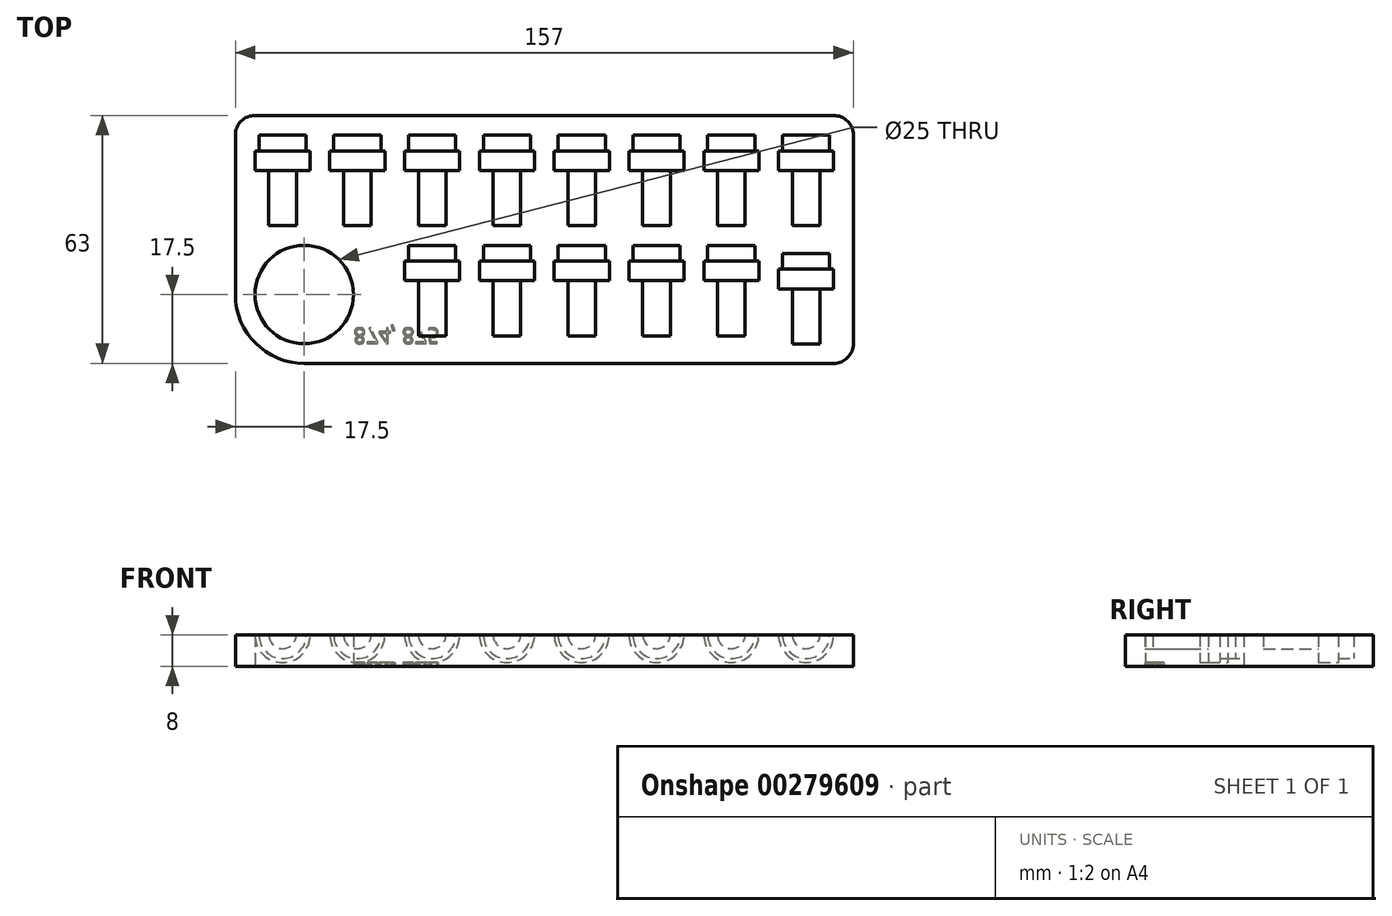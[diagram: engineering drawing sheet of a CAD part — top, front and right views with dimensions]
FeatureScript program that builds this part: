
annotation { "Feature Type Name" : "Feature", "Feature Type Description" : "" }
export const myFeature = defineFeature(function(context is Context, id is Id, definition is map)
    precondition{}
    {
        {
            var Q0;
            Q0=qCreatedBy(makeId("Top.planeOp"),FACE);
            var sketch = newSketch(context, id + "F0", { "sketchPlane" : qUnion([Q0])});
            skLineSegment(sketch, "E0.bottom", {"start": v(17.5, 0) * mm, "end": v(152, 0) * mm});
            skLineSegment(sketch, "E0.top", {"start": v(5, 63) * mm, "end": v(152, 63) * mm});
            skLineSegment(sketch, "E0.left", {"start": v(0, 17.5) * mm, "end": v(0, 58) * mm});
            skLineSegment(sketch, "E0.right", {"start": v(157, 5) * mm, "end": v(157, 58) * mm});
            skLineSegment(sketch, "E1.bottom", {"start": v(0, 0) * mm, "end": v(17.5, 0) * mm, "construction": true});
            skLineSegment(sketch, "E1.top", {"start": v(0, 17.5) * mm, "end": v(17.5, 17.5) * mm, "construction": true});
            skLineSegment(sketch, "E1.left", {"start": v(0, 0) * mm, "end": v(0, 17.5) * mm, "construction": true});
            skLineSegment(sketch, "E1.right", {"start": v(17.5, 0) * mm, "end": v(17.5, 17.5) * mm, "construction": true});
            skCircle(sketch, "E2", {"center": v(17.5, 17.5) * mm, "radius": 12.5 * mm});
            skPoint(sketch, "E3.visualSharp", {"position": v(0, 0) * mm});
            skArc(sketch, "E3.filletArc", {"start": v(0, 17.5) * mm, "mid": v(5.13, 5.13) * mm, "end": v(17.5, 0) * mm});
            skPoint(sketch, "E4.visualSharp", {"position": v(0, 63) * mm});
            skArc(sketch, "E4.filletArc", {"start": v(5, 63) * mm, "mid": v(1.46, 61.54) * mm, "end": v(0, 58) * mm});
            skPoint(sketch, "E5.visualSharp", {"position": v(157, 63) * mm});
            skArc(sketch, "E5.filletArc", {"start": v(157, 58) * mm, "mid": v(155.54, 61.54) * mm, "end": v(152, 63) * mm});
            skPoint(sketch, "E6.visualSharp", {"position": v(157, 0) * mm});
            skArc(sketch, "E6.filletArc", {"start": v(152, 0) * mm, "mid": v(155.54, 1.46) * mm, "end": v(157, 5) * mm});
            skSolve(sketch);
        }
        {
            var Q0;
            Q0=makeQuery(id+"F0.imprint","IMPRINT",FACE,{"disambiguationData":[TD([[makeQuery(id+"F0.imprint","IMPRINT",EDGE,{"derivedFrom":sQuery(id+"F0.wireOp",EDGE,"E0.bottom")}),1.0]])]});
            extrude(context, id + "F1", {"entities" : qUnion([Q0]), "depth" : 8 * mm});
        }
        {
            var Q0;
            Q0=makeQuery(id+"F1.opExtrude","CAP_FACE",FACE,{"disambiguationData":[OSD([sQuery(id+"F0.wireOp",EDGE,"E0.bottom"),sQuery(id+"F0.wireOp",EDGE,"E0.top"),sQuery(id+"F0.wireOp",EDGE,"E0.left"),sQuery(id+"F0.wireOp",EDGE,"E0.right"),sQuery(id+"F0.wireOp",EDGE,"E2"),sQuery(id+"F0.wireOp",EDGE,"E3.filletArc"),sQuery(id+"F0.wireOp",EDGE,"E4.filletArc"),sQuery(id+"F0.wireOp",EDGE,"E5.filletArc"),sQuery(id+"F0.wireOp",EDGE,"E6.filletArc")])],"isStart":false});
            var sketch = newSketch(context, id + "F2", { "sketchPlane" : qUnion([Q0])});
            skLineSegment(sketch, "E7.bottom", {"start": v(0, 0) * mm, "end": v(12, 0) * mm, "construction": true});
            skLineSegment(sketch, "E7.top", {"start": v(0, 35) * mm, "end": v(12, 35) * mm, "construction": true});
            skLineSegment(sketch, "E7.left", {"start": v(0, 0) * mm, "end": v(0, 35) * mm, "construction": true});
            skLineSegment(sketch, "E7.right", {"start": v(12, 0) * mm, "end": v(12, 35) * mm, "construction": true});
            skLineSegment(sketch, "E8.bottom", {"start": v(12, 35) * mm, "end": v(15.5, 35) * mm});
            skLineSegment(sketch, "E8.left", {"start": v(12, 35) * mm, "end": v(12, 49) * mm});
            skLineSegment(sketch, "E8.right", {"start": v(15.5, 35) * mm, "end": v(15.5, 49) * mm});
            skLineSegment(sketch, "E9.bottom", {"start": v(15.5, 49) * mm, "end": v(19, 49) * mm});
            skLineSegment(sketch, "E9.top", {"start": v(18, 54) * mm, "end": v(19, 54) * mm});
            skLineSegment(sketch, "E9.left", {"start": v(12, 49) * mm, "end": v(12, 54) * mm});
            skLineSegment(sketch, "E9.right", {"start": v(19, 49) * mm, "end": v(19, 54) * mm});
            skLineSegment(sketch, "E10.top", {"start": v(12, 58) * mm, "end": v(18, 58) * mm});
            skLineSegment(sketch, "E10.left", {"start": v(12, 54) * mm, "end": v(12, 58) * mm});
            skLineSegment(sketch, "E10.right", {"start": v(18, 54) * mm, "end": v(18, 58) * mm});
            skLineSegment(sketch, "E11", {"start": v(12, 35) * mm, "end": v(31, 35) * mm, "construction": true});
            skLineSegment(sketch, "E12.bottom", {"start": v(31, 35) * mm, "end": v(50, 35) * mm, "construction": true});
            skLineSegment(sketch, "E12.right", {"start": v(50, 35) * mm, "end": v(50, 30) * mm, "construction": true});
            skLineSegment(sketch, "E13.bottom", {"start": v(50, 35) * mm, "end": v(69, 35) * mm, "construction": true});
            skLineSegment(sketch, "E13.top", {"start": v(50, 30) * mm, "end": v(69, 30) * mm, "construction": true});
            skLineSegment(sketch, "E13.right", {"start": v(69, 35) * mm, "end": v(69, 30) * mm, "construction": true});
            skLineSegment(sketch, "E14.bottom", {"start": v(69, 35) * mm, "end": v(88, 35) * mm, "construction": true});
            skLineSegment(sketch, "E14.top", {"start": v(69, 30) * mm, "end": v(88, 30) * mm, "construction": true});
            skLineSegment(sketch, "E14.right", {"start": v(88, 35) * mm, "end": v(88, 30) * mm, "construction": true});
            skLineSegment(sketch, "E15.bottom", {"start": v(88, 35) * mm, "end": v(107, 35) * mm, "construction": true});
            skLineSegment(sketch, "E15.top", {"start": v(88, 30) * mm, "end": v(107, 30) * mm, "construction": true});
            skLineSegment(sketch, "E15.right", {"start": v(107, 35) * mm, "end": v(107, 30) * mm, "construction": true});
            skLineSegment(sketch, "E16.bottom", {"start": v(107, 35) * mm, "end": v(126, 35) * mm, "construction": true});
            skLineSegment(sketch, "E16.top", {"start": v(107, 30) * mm, "end": v(126, 30) * mm, "construction": true});
            skLineSegment(sketch, "E16.right", {"start": v(126, 35) * mm, "end": v(126, 30) * mm, "construction": true});
            skLineSegment(sketch, "E17.bottom", {"start": v(107, 35) * mm, "end": v(110.5, 35) * mm});
            skLineSegment(sketch, "E17.left", {"start": v(107, 35) * mm, "end": v(107, 49) * mm});
            skLineSegment(sketch, "E17.right", {"start": v(110.5, 35) * mm, "end": v(110.5, 49) * mm});
            skLineSegment(sketch, "E18.bottom", {"start": v(110.5, 49) * mm, "end": v(114, 49) * mm});
            skLineSegment(sketch, "E18.top", {"start": v(113, 54) * mm, "end": v(114, 54) * mm});
            skLineSegment(sketch, "E18.left", {"start": v(107, 49) * mm, "end": v(107, 54) * mm});
            skLineSegment(sketch, "E18.right", {"start": v(114, 49) * mm, "end": v(114, 54) * mm});
            skLineSegment(sketch, "E19.top", {"start": v(107, 58) * mm, "end": v(113, 58) * mm});
            skLineSegment(sketch, "E19.left", {"start": v(107, 54) * mm, "end": v(107, 58) * mm});
            skLineSegment(sketch, "E19.right", {"start": v(113, 54) * mm, "end": v(113, 58) * mm});
            skLineSegment(sketch, "E20.bottom", {"start": v(50, 35) * mm, "end": v(53.5, 35) * mm});
            skLineSegment(sketch, "E20.left", {"start": v(50, 35) * mm, "end": v(50, 49) * mm});
            skLineSegment(sketch, "E20.right", {"start": v(53.5, 35) * mm, "end": v(53.5, 49) * mm});
            skLineSegment(sketch, "E21.bottom", {"start": v(53.5, 49) * mm, "end": v(57, 49) * mm});
            skLineSegment(sketch, "E21.top", {"start": v(56, 54) * mm, "end": v(57, 54) * mm});
            skLineSegment(sketch, "E21.left", {"start": v(50, 49) * mm, "end": v(50, 54) * mm});
            skLineSegment(sketch, "E21.right", {"start": v(57, 49) * mm, "end": v(57, 54) * mm});
            skLineSegment(sketch, "E22.top", {"start": v(50, 58) * mm, "end": v(56, 58) * mm});
            skLineSegment(sketch, "E22.left", {"start": v(50, 54) * mm, "end": v(50, 58) * mm});
            skLineSegment(sketch, "E22.right", {"start": v(56, 54) * mm, "end": v(56, 58) * mm});
            skLineSegment(sketch, "E23.bottom", {"start": v(88, 35) * mm, "end": v(91.5, 35) * mm});
            skLineSegment(sketch, "E23.left", {"start": v(88, 35) * mm, "end": v(88, 49) * mm});
            skLineSegment(sketch, "E23.right", {"start": v(91.5, 35) * mm, "end": v(91.5, 49) * mm});
            skLineSegment(sketch, "E24.bottom", {"start": v(91.5, 49) * mm, "end": v(95, 49) * mm});
            skLineSegment(sketch, "E24.top", {"start": v(94, 54) * mm, "end": v(95, 54) * mm});
            skLineSegment(sketch, "E24.left", {"start": v(88, 49) * mm, "end": v(88, 54) * mm});
            skLineSegment(sketch, "E24.right", {"start": v(95, 49) * mm, "end": v(95, 54) * mm});
            skLineSegment(sketch, "E25.top", {"start": v(88, 58) * mm, "end": v(94, 58) * mm});
            skLineSegment(sketch, "E25.left", {"start": v(88, 54) * mm, "end": v(88, 58) * mm});
            skLineSegment(sketch, "E25.right", {"start": v(94, 54) * mm, "end": v(94, 58) * mm});
            skLineSegment(sketch, "E26.bottom", {"start": v(69, 35) * mm, "end": v(72.5, 35) * mm});
            skLineSegment(sketch, "E26.left", {"start": v(69, 35) * mm, "end": v(69, 49) * mm});
            skLineSegment(sketch, "E26.right", {"start": v(72.5, 35) * mm, "end": v(72.5, 49) * mm});
            skLineSegment(sketch, "E27.bottom", {"start": v(72.5, 49) * mm, "end": v(76, 49) * mm});
            skLineSegment(sketch, "E27.top", {"start": v(75, 54) * mm, "end": v(76, 54) * mm});
            skLineSegment(sketch, "E27.left", {"start": v(69, 49) * mm, "end": v(69, 54) * mm});
            skLineSegment(sketch, "E27.right", {"start": v(76, 49) * mm, "end": v(76, 54) * mm});
            skLineSegment(sketch, "E28.top", {"start": v(69, 58) * mm, "end": v(75, 58) * mm});
            skLineSegment(sketch, "E28.left", {"start": v(69, 54) * mm, "end": v(69, 58) * mm});
            skLineSegment(sketch, "E28.right", {"start": v(75, 54) * mm, "end": v(75, 58) * mm});
            skLineSegment(sketch, "E29.bottom", {"start": v(31, 35) * mm, "end": v(34.5, 35) * mm});
            skLineSegment(sketch, "E29.left", {"start": v(31, 35) * mm, "end": v(31, 49) * mm});
            skLineSegment(sketch, "E29.right", {"start": v(34.5, 35) * mm, "end": v(34.5, 49) * mm});
            skLineSegment(sketch, "E30.bottom", {"start": v(34.5, 49) * mm, "end": v(38, 49) * mm});
            skLineSegment(sketch, "E30.top", {"start": v(37, 54) * mm, "end": v(38, 54) * mm});
            skLineSegment(sketch, "E30.left", {"start": v(31, 49) * mm, "end": v(31, 54) * mm});
            skLineSegment(sketch, "E30.right", {"start": v(38, 49) * mm, "end": v(38, 54) * mm});
            skLineSegment(sketch, "E31.top", {"start": v(31, 58) * mm, "end": v(37, 58) * mm});
            skLineSegment(sketch, "E31.left", {"start": v(31, 54) * mm, "end": v(31, 58) * mm});
            skLineSegment(sketch, "E31.right", {"start": v(37, 54) * mm, "end": v(37, 58) * mm});
            skLineSegment(sketch, "E32.bottom", {"start": v(50, 7) * mm, "end": v(53.5, 7) * mm});
            skLineSegment(sketch, "E32.left", {"start": v(50, 7) * mm, "end": v(50, 21) * mm});
            skLineSegment(sketch, "E32.right", {"start": v(53.5, 7) * mm, "end": v(53.5, 21) * mm});
            skLineSegment(sketch, "E33.bottom", {"start": v(53.5, 21) * mm, "end": v(57, 21) * mm});
            skLineSegment(sketch, "E33.top", {"start": v(56, 26) * mm, "end": v(57, 26) * mm});
            skLineSegment(sketch, "E33.left", {"start": v(50, 21) * mm, "end": v(50, 26) * mm});
            skLineSegment(sketch, "E33.right", {"start": v(57, 21) * mm, "end": v(57, 26) * mm});
            skLineSegment(sketch, "E34.top", {"start": v(50, 30) * mm, "end": v(56, 30) * mm});
            skLineSegment(sketch, "E34.left", {"start": v(50, 26) * mm, "end": v(50, 30) * mm});
            skLineSegment(sketch, "E34.right", {"start": v(56, 26) * mm, "end": v(56, 30) * mm});
            skLineSegment(sketch, "E35.bottom", {"start": v(88, 7) * mm, "end": v(91.5, 7) * mm});
            skLineSegment(sketch, "E35.left", {"start": v(88, 7) * mm, "end": v(88, 21) * mm});
            skLineSegment(sketch, "E35.right", {"start": v(91.5, 7) * mm, "end": v(91.5, 21) * mm});
            skLineSegment(sketch, "E36.bottom", {"start": v(91.5, 21) * mm, "end": v(95, 21) * mm});
            skLineSegment(sketch, "E36.top", {"start": v(94, 26) * mm, "end": v(95, 26) * mm});
            skLineSegment(sketch, "E36.left", {"start": v(88, 21) * mm, "end": v(88, 26) * mm});
            skLineSegment(sketch, "E36.right", {"start": v(95, 21) * mm, "end": v(95, 26) * mm});
            skLineSegment(sketch, "E37.top", {"start": v(88, 30) * mm, "end": v(94, 30) * mm});
            skLineSegment(sketch, "E37.left", {"start": v(88, 26) * mm, "end": v(88, 30) * mm});
            skLineSegment(sketch, "E37.right", {"start": v(94, 26) * mm, "end": v(94, 30) * mm});
            skLineSegment(sketch, "E38.bottom", {"start": v(107, 7) * mm, "end": v(110.5, 7) * mm});
            skLineSegment(sketch, "E38.left", {"start": v(107, 7) * mm, "end": v(107, 21) * mm});
            skLineSegment(sketch, "E38.right", {"start": v(110.5, 7) * mm, "end": v(110.5, 21) * mm});
            skLineSegment(sketch, "E39.bottom", {"start": v(110.5, 21) * mm, "end": v(114, 21) * mm});
            skLineSegment(sketch, "E39.top", {"start": v(113, 26) * mm, "end": v(114, 26) * mm});
            skLineSegment(sketch, "E39.left", {"start": v(107, 21) * mm, "end": v(107, 26) * mm});
            skLineSegment(sketch, "E39.right", {"start": v(114, 21) * mm, "end": v(114, 26) * mm});
            skLineSegment(sketch, "E40.top", {"start": v(107, 30) * mm, "end": v(113, 30) * mm});
            skLineSegment(sketch, "E40.left", {"start": v(107, 26) * mm, "end": v(107, 30) * mm});
            skLineSegment(sketch, "E40.right", {"start": v(113, 26) * mm, "end": v(113, 30) * mm});
            skLineSegment(sketch, "E41.bottom", {"start": v(126, 7) * mm, "end": v(129.5, 7) * mm});
            skLineSegment(sketch, "E41.left", {"start": v(126, 7) * mm, "end": v(126, 21) * mm});
            skLineSegment(sketch, "E41.right", {"start": v(129.5, 7) * mm, "end": v(129.5, 21) * mm});
            skLineSegment(sketch, "E42.bottom", {"start": v(129.5, 21) * mm, "end": v(133, 21) * mm});
            skLineSegment(sketch, "E42.top", {"start": v(132, 26) * mm, "end": v(133, 26) * mm});
            skLineSegment(sketch, "E42.left", {"start": v(126, 21) * mm, "end": v(126, 26) * mm});
            skLineSegment(sketch, "E42.right", {"start": v(133, 21) * mm, "end": v(133, 26) * mm});
            skLineSegment(sketch, "E43.top", {"start": v(126, 30) * mm, "end": v(132, 30) * mm});
            skLineSegment(sketch, "E43.left", {"start": v(126, 26) * mm, "end": v(126, 30) * mm});
            skLineSegment(sketch, "E43.right", {"start": v(132, 26) * mm, "end": v(132, 30) * mm});
            skLineSegment(sketch, "E44.bottom", {"start": v(69, 7) * mm, "end": v(72.5, 7) * mm});
            skLineSegment(sketch, "E44.left", {"start": v(69, 7) * mm, "end": v(69, 21) * mm});
            skLineSegment(sketch, "E44.right", {"start": v(72.5, 7) * mm, "end": v(72.5, 21) * mm});
            skLineSegment(sketch, "E45.bottom", {"start": v(72.5, 21) * mm, "end": v(76, 21) * mm});
            skLineSegment(sketch, "E45.top", {"start": v(75, 26) * mm, "end": v(76, 26) * mm});
            skLineSegment(sketch, "E45.left", {"start": v(69, 21) * mm, "end": v(69, 26) * mm});
            skLineSegment(sketch, "E45.right", {"start": v(76, 21) * mm, "end": v(76, 26) * mm});
            skLineSegment(sketch, "E46.top", {"start": v(69, 30) * mm, "end": v(75, 30) * mm});
            skLineSegment(sketch, "E46.left", {"start": v(69, 26) * mm, "end": v(69, 30) * mm});
            skLineSegment(sketch, "E46.right", {"start": v(75, 26) * mm, "end": v(75, 30) * mm});
            skLineSegment(sketch, "E47.bottom", {"start": v(126, 35) * mm, "end": v(129.5, 35) * mm});
            skLineSegment(sketch, "E47.left", {"start": v(126, 35) * mm, "end": v(126, 49) * mm});
            skLineSegment(sketch, "E47.right", {"start": v(129.5, 35) * mm, "end": v(129.5, 49) * mm});
            skLineSegment(sketch, "E48.bottom", {"start": v(129.5, 49) * mm, "end": v(133, 49) * mm});
            skLineSegment(sketch, "E48.top", {"start": v(132, 54) * mm, "end": v(133, 54) * mm});
            skLineSegment(sketch, "E48.left", {"start": v(126, 49) * mm, "end": v(126, 54) * mm});
            skLineSegment(sketch, "E48.right", {"start": v(133, 49) * mm, "end": v(133, 54) * mm});
            skLineSegment(sketch, "E49.top", {"start": v(126, 58) * mm, "end": v(132, 58) * mm});
            skLineSegment(sketch, "E49.left", {"start": v(126, 54) * mm, "end": v(126, 58) * mm});
            skLineSegment(sketch, "E49.right", {"start": v(132, 54) * mm, "end": v(132, 58) * mm});
            skLineSegment(sketch, "E50.bottom", {"start": v(126, 35) * mm, "end": v(145, 35) * mm, "construction": true});
            skLineSegment(sketch, "E50.right", {"start": v(145, 35) * mm, "end": v(145, 27.94) * mm, "construction": true});
            skLineSegment(sketch, "E51.bottom", {"start": v(145, 4.94) * mm, "end": v(148.5, 4.94) * mm});
            skLineSegment(sketch, "E51.left", {"start": v(145, 4.94) * mm, "end": v(145, 18.94) * mm});
            skLineSegment(sketch, "E51.right", {"start": v(148.5, 4.94) * mm, "end": v(148.5, 18.94) * mm});
            skLineSegment(sketch, "E52.bottom", {"start": v(148.5, 18.94) * mm, "end": v(152, 18.94) * mm});
            skLineSegment(sketch, "E52.top", {"start": v(151, 23.94) * mm, "end": v(152, 23.94) * mm});
            skLineSegment(sketch, "E52.left", {"start": v(145, 18.94) * mm, "end": v(145, 23.94) * mm});
            skLineSegment(sketch, "E52.right", {"start": v(152, 18.94) * mm, "end": v(152, 23.94) * mm});
            skLineSegment(sketch, "E53.top", {"start": v(145, 27.94) * mm, "end": v(151, 27.94) * mm});
            skLineSegment(sketch, "E53.left", {"start": v(145, 23.94) * mm, "end": v(145, 27.94) * mm});
            skLineSegment(sketch, "E53.right", {"start": v(151, 23.94) * mm, "end": v(151, 27.94) * mm});
            skLineSegment(sketch, "E54.bottom", {"start": v(145, 35) * mm, "end": v(148.5, 35) * mm});
            skLineSegment(sketch, "E54.left", {"start": v(145, 35) * mm, "end": v(145, 49) * mm});
            skLineSegment(sketch, "E54.right", {"start": v(148.5, 35) * mm, "end": v(148.5, 49) * mm});
            skLineSegment(sketch, "E55.bottom", {"start": v(148.5, 49) * mm, "end": v(152, 49) * mm});
            skLineSegment(sketch, "E55.top", {"start": v(151, 54) * mm, "end": v(152, 54) * mm});
            skLineSegment(sketch, "E55.left", {"start": v(145, 49) * mm, "end": v(145, 54) * mm});
            skLineSegment(sketch, "E55.right", {"start": v(152, 49) * mm, "end": v(152, 54) * mm});
            skLineSegment(sketch, "E56.top", {"start": v(145, 58) * mm, "end": v(151, 58) * mm});
            skLineSegment(sketch, "E56.left", {"start": v(145, 54) * mm, "end": v(145, 58) * mm});
            skLineSegment(sketch, "E56.right", {"start": v(151, 54) * mm, "end": v(151, 58) * mm});
            skSolve(sketch);
        }
        {
            var Q0;
            Q0=makeQuery(id+"F2.imprint","IMPRINT",FACE,{"disambiguationData":[TD([[makeQuery(id+"F2.imprint","IMPRINT",EDGE,{"derivedFrom":sQuery(id+"F2.wireOp",EDGE,"E8.bottom")}),1.0]])]});
            var Q1;
            Q1=sQuery(id+"F2.wireOp",EDGE,"E8.left");
            revolve(context, id + "F3", {"operationType" : NewBodyOperationType.REMOVE, "entities" : qUnion([Q0]), "axis" : qUnion([Q1]), "revolveType" : RevolveType.FULL, "oppositeDirection" : true});
        }
        {
            var Q0;
            Q0=makeQuery(id+"F2.imprint","IMPRINT",FACE,{"disambiguationData":[TD([[makeQuery(id+"F2.imprint","IMPRINT",EDGE,{"derivedFrom":sQuery(id+"F2.wireOp",EDGE,"E29.bottom")}),1.0]])]});
            var Q1;
            Q1=sQuery(id+"F2.wireOp",EDGE,"E29.left");
            revolve(context, id + "F4", {"operationType" : NewBodyOperationType.REMOVE, "entities" : qUnion([Q0]), "axis" : qUnion([Q1]), "revolveType" : RevolveType.FULL, "oppositeDirection" : true});
        }
        {
            var Q0;
            Q0=makeQuery(id+"F2.imprint","IMPRINT",FACE,{"disambiguationData":[TD([[makeQuery(id+"F2.imprint","IMPRINT",EDGE,{"derivedFrom":sQuery(id+"F2.wireOp",EDGE,"E32.bottom")}),1.0]])]});
            var Q1;
            Q1=makeQuery(id+"F2.imprint","IMPRINT",FACE,{"disambiguationData":[TD([[makeQuery(id+"F2.imprint","IMPRINT",EDGE,{"derivedFrom":sQuery(id+"F2.wireOp",EDGE,"E20.bottom")}),1.0]])]});
            var Q2;
            Q2=sQuery(id+"F2.wireOp",EDGE,"E20.left");
            revolve(context, id + "F5", {"operationType" : NewBodyOperationType.REMOVE, "entities" : qUnion([Q0, Q1]), "axis" : qUnion([Q2]), "revolveType" : RevolveType.FULL, "oppositeDirection" : true});
        }
        {
            var Q0;
            Q0=makeQuery(id+"F2.imprint","IMPRINT",FACE,{"disambiguationData":[TD([[makeQuery(id+"F2.imprint","IMPRINT",EDGE,{"derivedFrom":sQuery(id+"F2.wireOp",EDGE,"E44.bottom")}),1.0]])]});
            var Q1;
            Q1=makeQuery(id+"F2.imprint","IMPRINT",FACE,{"disambiguationData":[TD([[makeQuery(id+"F2.imprint","IMPRINT",EDGE,{"derivedFrom":sQuery(id+"F2.wireOp",EDGE,"E26.bottom")}),1.0]])]});
            var Q2;
            Q2=sQuery(id+"F2.wireOp",EDGE,"E26.left");
            revolve(context, id + "F6", {"operationType" : NewBodyOperationType.REMOVE, "entities" : qUnion([Q0, Q1]), "axis" : qUnion([Q2]), "revolveType" : RevolveType.FULL, "oppositeDirection" : true});
        }
        {
            var Q0;
            Q0=makeQuery(id+"F2.imprint","IMPRINT",FACE,{"disambiguationData":[TD([[makeQuery(id+"F2.imprint","IMPRINT",EDGE,{"derivedFrom":sQuery(id+"F2.wireOp",EDGE,"E35.bottom")}),1.0]])]});
            var Q1;
            Q1=makeQuery(id+"F2.imprint","IMPRINT",FACE,{"disambiguationData":[TD([[makeQuery(id+"F2.imprint","IMPRINT",EDGE,{"derivedFrom":sQuery(id+"F2.wireOp",EDGE,"E23.bottom")}),1.0]])]});
            var Q2;
            Q2=sQuery(id+"F2.wireOp",EDGE,"E23.left");
            revolve(context, id + "F7", {"operationType" : NewBodyOperationType.REMOVE, "entities" : qUnion([Q0, Q1]), "axis" : qUnion([Q2]), "revolveType" : RevolveType.FULL, "oppositeDirection" : true});
        }
        {
            var Q0;
            Q0=makeQuery(id+"F2.imprint","IMPRINT",FACE,{"disambiguationData":[TD([[makeQuery(id+"F2.imprint","IMPRINT",EDGE,{"derivedFrom":sQuery(id+"F2.wireOp",EDGE,"E38.bottom")}),1.0]])]});
            var Q1;
            Q1=makeQuery(id+"F2.imprint","IMPRINT",FACE,{"disambiguationData":[TD([[makeQuery(id+"F2.imprint","IMPRINT",EDGE,{"derivedFrom":sQuery(id+"F2.wireOp",EDGE,"E17.bottom")}),1.0]])]});
            var Q2;
            Q2=sQuery(id+"F2.wireOp",EDGE,"E17.left");
            revolve(context, id + "F8", {"operationType" : NewBodyOperationType.REMOVE, "entities" : qUnion([Q0, Q1]), "axis" : qUnion([Q2]), "revolveType" : RevolveType.FULL, "oppositeDirection" : true});
        }
        {
            var Q0;
            Q0=makeQuery(id+"F2.imprint","IMPRINT",FACE,{"disambiguationData":[TD([[makeQuery(id+"F2.imprint","IMPRINT",EDGE,{"derivedFrom":sQuery(id+"F2.wireOp",EDGE,"E41.bottom")}),1.0]])]});
            var Q1;
            Q1=makeQuery(id+"F2.imprint","IMPRINT",FACE,{"disambiguationData":[TD([[makeQuery(id+"F2.imprint","IMPRINT",EDGE,{"derivedFrom":sQuery(id+"F2.wireOp",EDGE,"E47.bottom")}),1.0]])]});
            var Q2;
            Q2=sQuery(id+"F2.wireOp",EDGE,"E47.left");
            revolve(context, id + "F9", {"operationType" : NewBodyOperationType.REMOVE, "entities" : qUnion([Q0, Q1]), "axis" : qUnion([Q2]), "revolveType" : RevolveType.FULL, "oppositeDirection" : true});
        }
        {
            var Q0;
            Q0=makeQuery(id+"F2.imprint","IMPRINT",FACE,{"disambiguationData":[TD([[makeQuery(id+"F2.imprint","IMPRINT",EDGE,{"derivedFrom":sQuery(id+"F2.wireOp",EDGE,"E51.bottom")}),1.0]])]});
            var Q1;
            Q1=makeQuery(id+"F2.imprint","IMPRINT",FACE,{"disambiguationData":[TD([[makeQuery(id+"F2.imprint","IMPRINT",EDGE,{"derivedFrom":sQuery(id+"F2.wireOp",EDGE,"E54.bottom")}),1.0]])]});
            var Q2;
            Q2=sQuery(id+"F2.wireOp",EDGE,"E54.left");
            revolve(context, id + "F10", {"operationType" : NewBodyOperationType.REMOVE, "entities" : qUnion([Q0, Q1]), "axis" : qUnion([Q2]), "revolveType" : RevolveType.FULL, "oppositeDirection" : true});
        }
        {
            var Q0;
            Q0=makeQuery(id+"F1.opExtrude","CAP_FACE",FACE,{"disambiguationData":[OSD([sQuery(id+"F0.wireOp",EDGE,"E0.bottom"),sQuery(id+"F0.wireOp",EDGE,"E0.top"),sQuery(id+"F0.wireOp",EDGE,"E0.left"),sQuery(id+"F0.wireOp",EDGE,"E0.right"),sQuery(id+"F0.wireOp",EDGE,"E2"),sQuery(id+"F0.wireOp",EDGE,"E3.filletArc"),sQuery(id+"F0.wireOp",EDGE,"E4.filletArc"),sQuery(id+"F0.wireOp",EDGE,"E5.filletArc"),sQuery(id+"F0.wireOp",EDGE,"E6.filletArc")])],"isStart":true});
            var sketch = newSketch(context, id + "F11", { "sketchPlane" : qUnion([Q0])});
            skLineSegment(sketch, "E57.bottom", {"start": v(0, 0) * mm, "end": v(30, 0) * mm, "construction": true});
            skLineSegment(sketch, "E57.top", {"start": v(0, -5) * mm, "end": v(30, -5) * mm, "construction": true});
            skLineSegment(sketch, "E57.left", {"start": v(0, 0) * mm, "end": v(0, -5) * mm, "construction": true});
            skLineSegment(sketch, "E57.right", {"start": v(30, 0) * mm, "end": v(30, -5) * mm, "construction": true});
            skText(sketch, "E58", { "text": "874, 875", "fontName": "OpenSans-Regular.ttf"});
            const initialGuessF11  = {"E58": [0.03, -0.009, 1, 0, 0.004]};
            skSetInitialGuess(sketch, initialGuessF11);
            skSolve(sketch);
        }
        {
            var Q0;
            Q0 = qSketchRegion(id + "F11", true);
            extrude(context, id + "F12", {"entities" : qUnion([Q0]), "operationType" : NewBodyOperationType.REMOVE, "oppositeDirection" : true, "depth" : 1 * mm});
        }
    });
